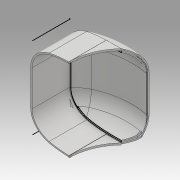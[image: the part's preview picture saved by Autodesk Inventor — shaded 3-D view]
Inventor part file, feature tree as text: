
AUTODESK INVENTOR PART (.ipt)
format: ipt  version: 2017 (Build 210142000, 142)  size: 410,112 bytes
history: native  units: mm
features: sketch x4, other x3, projected_geometry x2, sweep x1
ambient origin geometry x8: Origin, YZ Plane, XZ Plane, XY Plane, X Axis, Y Axis, Z Axis, Center Point
bodies: Solid1 (feature_tree)
feature tree (10):
  other  "Pelo.ipt"
  sweep  "Sweep1"
  sketch  "Sketch3"
  other  "Solid1::Pelo.ipt"
  other  "TaggingFeature1"
  sketch  "Sketch60"
  sketch  "Sketch2"  dims[d0=11.0mm d1=0.0mm d2=0.0mm]
  projected_geometry  "Projected Loop1"
  sketch  "3D Sketch1"
  projected_geometry  "Projected Loop2"
